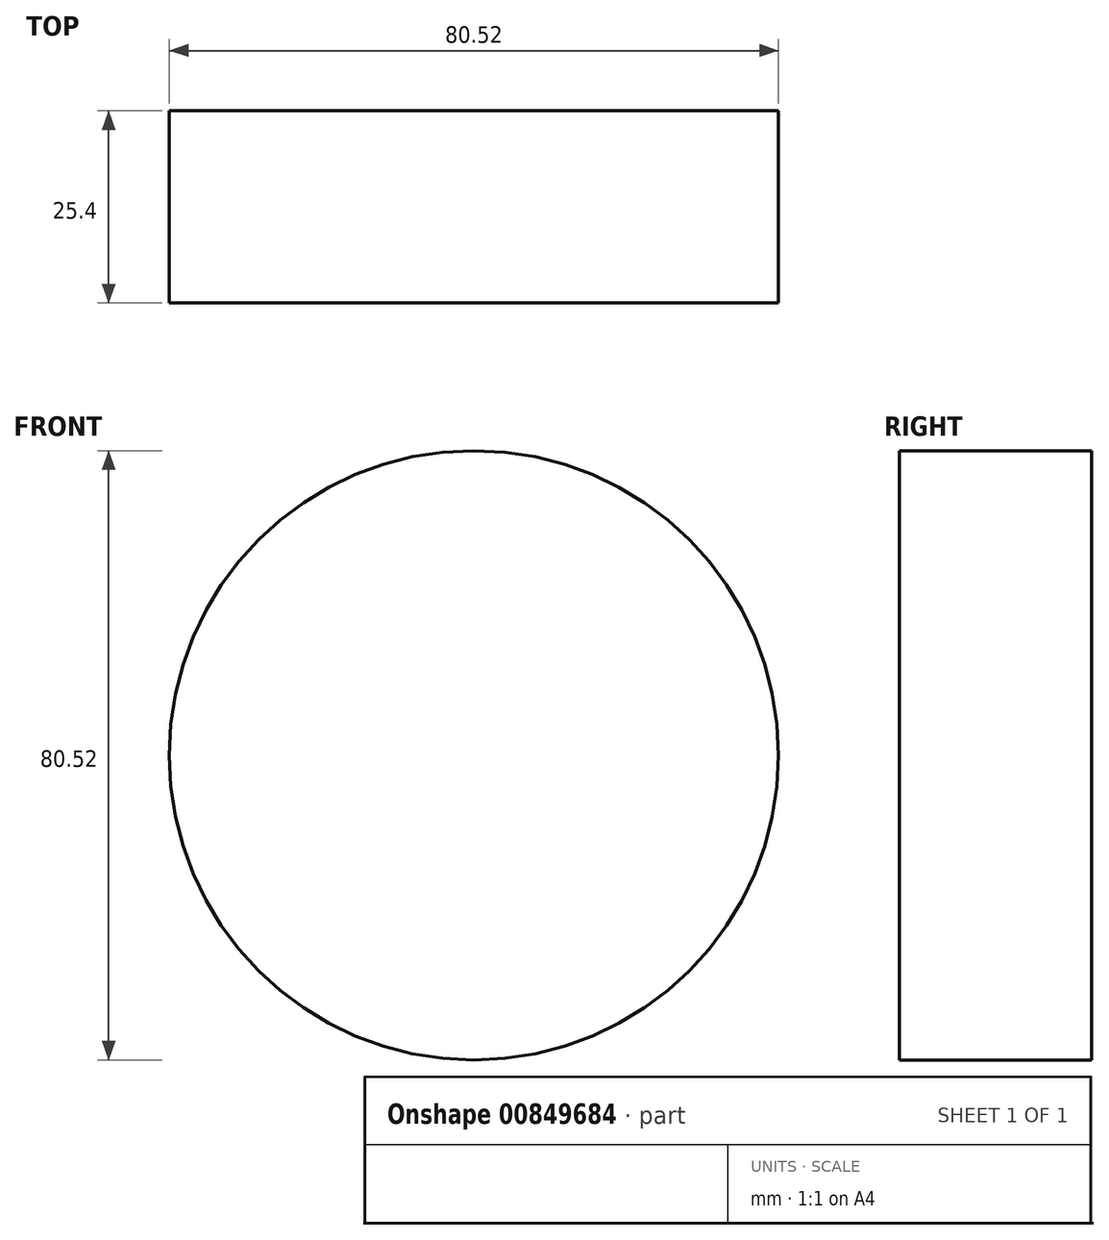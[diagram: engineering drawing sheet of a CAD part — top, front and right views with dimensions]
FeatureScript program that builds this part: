
annotation { "Feature Type Name" : "Feature", "Feature Type Description" : "" }
export const myFeature = defineFeature(function(context is Context, id is Id, definition is map)
    precondition{}
    {
        {
            var Q0;
            Q0=qCreatedBy(makeId("Front.planeOp"),FACE);
            var sketch = newSketch(context, id + "F0", { "sketchPlane" : qUnion([Q0])});
            skCircle(sketch, "E0", {"center": v(0, 0) * mm, "radius": 40.26 * mm});
            skSolve(sketch);
        }
        {
            var Q0;
            Q0=makeQuery(id+"F0.imprint","IMPRINT",FACE,{"disambiguationData":[TD([[makeQuery(id+"F0.imprint","IMPRINT",EDGE,{"derivedFrom":sQuery(id+"F0.wireOp",EDGE,"E0")}),1.0]])]});
            extrude(context, id + "F1", {"entities" : qUnion([Q0]), "depth" : 25.4 * mm, "offsetDistance" : 25.4 * mm});
        }
    });
